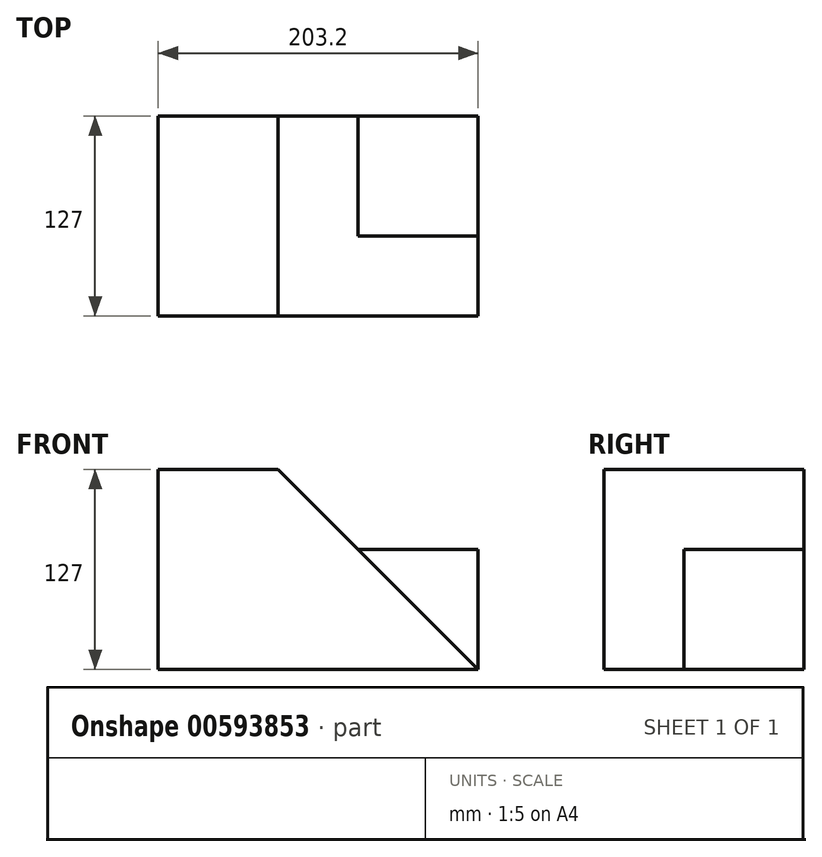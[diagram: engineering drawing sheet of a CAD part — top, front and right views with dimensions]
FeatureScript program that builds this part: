
annotation { "Feature Type Name" : "Feature", "Feature Type Description" : "" }
export const myFeature = defineFeature(function(context is Context, id is Id, definition is map)
    precondition{}
    {
        {
            var Q0;
            Q0=qCreatedBy(makeId("Front.planeOp"),FACE);
            var sketch = newSketch(context, id + "F0", { "sketchPlane" : qUnion([Q0])});
            skLineSegment(sketch, "E0.bottom", {"start": v(0, 0) * mm, "end": v(203.2, 0) * mm});
            skLineSegment(sketch, "E0.top", {"start": v(0, 127) * mm, "end": v(203.2, 127) * mm});
            skLineSegment(sketch, "E0.left", {"start": v(0, 0) * mm, "end": v(0, 127) * mm});
            skLineSegment(sketch, "E0.right", {"start": v(203.2, 0) * mm, "end": v(203.2, 127) * mm});
            skLineSegment(sketch, "E1", {"start": v(76.2, 127) * mm, "end": v(203.2, 0) * mm});
            skLineSegment(sketch, "E2", {"start": v(203.2, 127) * mm, "end": v(127, 127) * mm, "construction": true});
            skLineSegment(sketch, "E3", {"start": v(127, 127) * mm, "end": v(127, 76.2) * mm, "construction": true});
            skLineSegment(sketch, "E4", {"start": v(127, 76.2) * mm, "end": v(203.2, 76.2) * mm});
            skSolve(sketch);
        }
        {
            var Q0;
            {var subQ5=sQuery(id+"F0.wireOp",EDGE,"E0.bottom");Q0=makeQuery(id+"F0.imprint","IMPRINT",FACE,{"disambiguationData":[TD([[makeQuery(id+"F0.imprint","IMPRINT",EDGE,{"derivedFrom":subQ5}),1.0]])]});}
            extrude(context, id + "F1", {"entities" : qUnion([Q0]), "depth" : 127 * mm, "offsetDistance" : 25.4 * mm});
        }
        {
            var Q0;
            {var subQ3=sQuery(id+"F0.wireOp",EDGE,"E4");Q0=makeQuery(id+"F0.imprint","IMPRINT",FACE,{"disambiguationData":[TD([[makeQuery(id+"F0.imprint","IMPRINT",EDGE,{"derivedFrom":subQ3}),-1.0]])]});}
            extrude(context, id + "F2", {"entities" : qUnion([Q0]), "operationType" : NewBodyOperationType.ADD, "depth" : 76.2 * mm, "offsetDistance" : 25.4 * mm});
        }
    });
